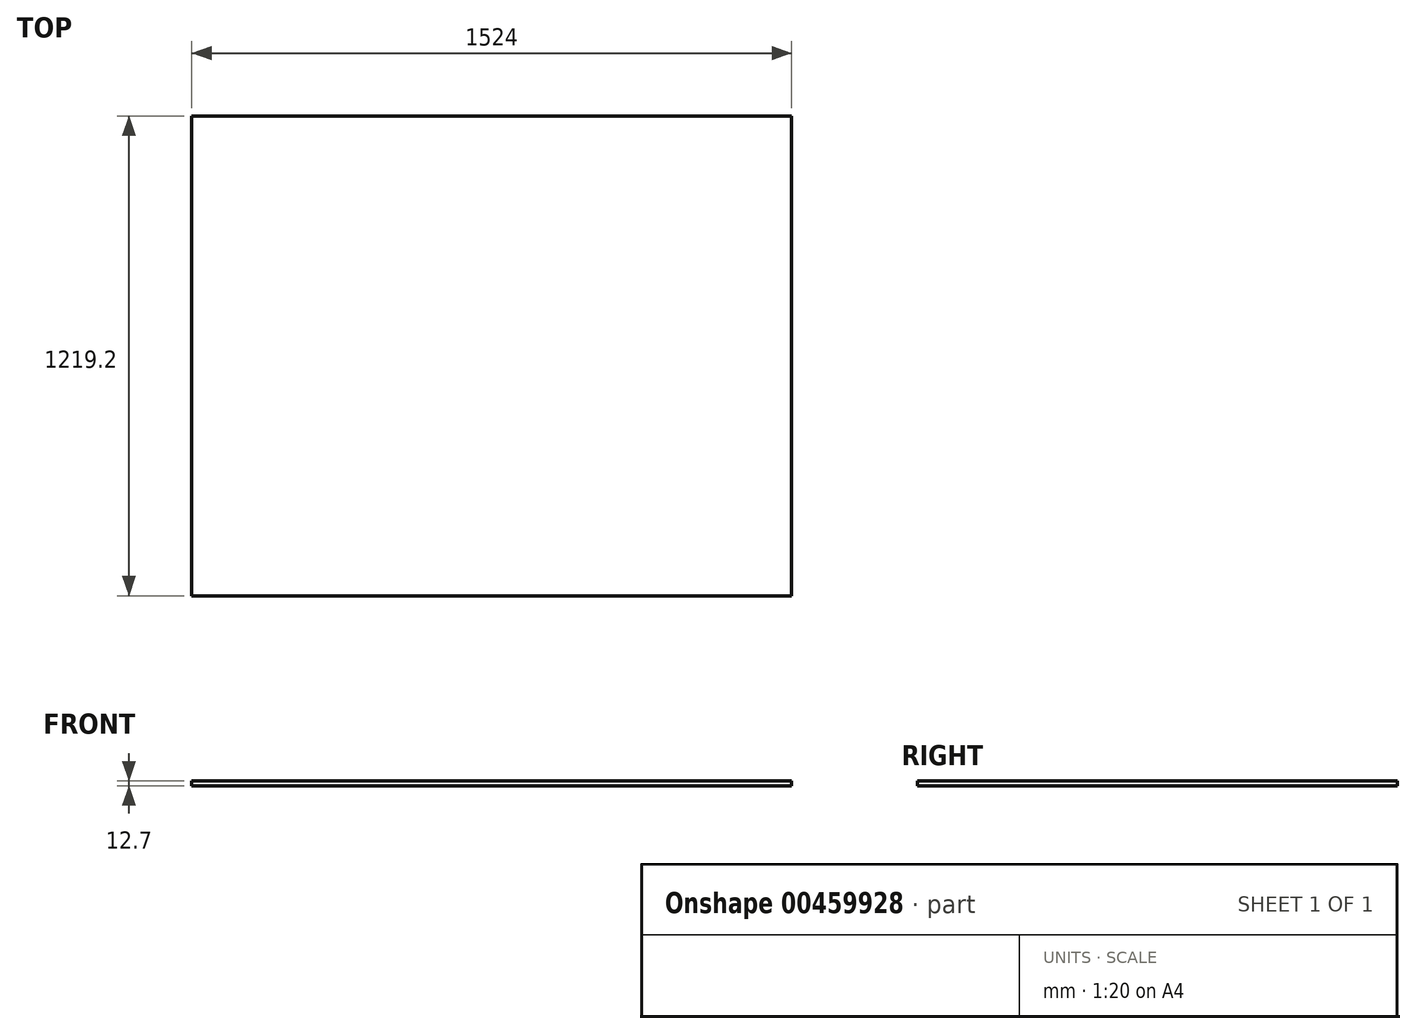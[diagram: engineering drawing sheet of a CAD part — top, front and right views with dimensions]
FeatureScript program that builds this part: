
annotation { "Feature Type Name" : "Feature", "Feature Type Description" : "" }
export const myFeature = defineFeature(function(context is Context, id is Id, definition is map)
    precondition{}
    {
        {
            var Q0;
            Q0=qCreatedBy(makeId("Top.planeOp"),FACE);
            var sketch = newSketch(context, id + "F0", { "sketchPlane" : qUnion([Q0])});
            skLineSegment(sketch, "E0.bottom", {"start": v(762, 609.6) * mm, "end": v(-762, 609.6) * mm});
            skLineSegment(sketch, "E0.top", {"start": v(762, -609.6) * mm, "end": v(-762, -609.6) * mm});
            skLineSegment(sketch, "E0.left", {"start": v(762, 609.6) * mm, "end": v(762, -609.6) * mm});
            skLineSegment(sketch, "E0.right", {"start": v(-762, 609.6) * mm, "end": v(-762, -609.6) * mm});
            skPoint(sketch, "E0.middle", {"position": v(0, 0) * mm});
            skSolve(sketch);
        }
        {
            var Q0;
            Q0=makeQuery(id+"F0.imprint","IMPRINT",FACE,{"disambiguationData":[TD([[makeQuery(id+"F0.imprint","IMPRINT",EDGE,{"derivedFrom":sQuery(id+"F0.wireOp",EDGE,"E0.bottom")}),1.0]])]});
            extrude(context, id + "F1", {"entities" : qUnion([Q0]), "depth" : 12.7 * mm});
        }
    });
